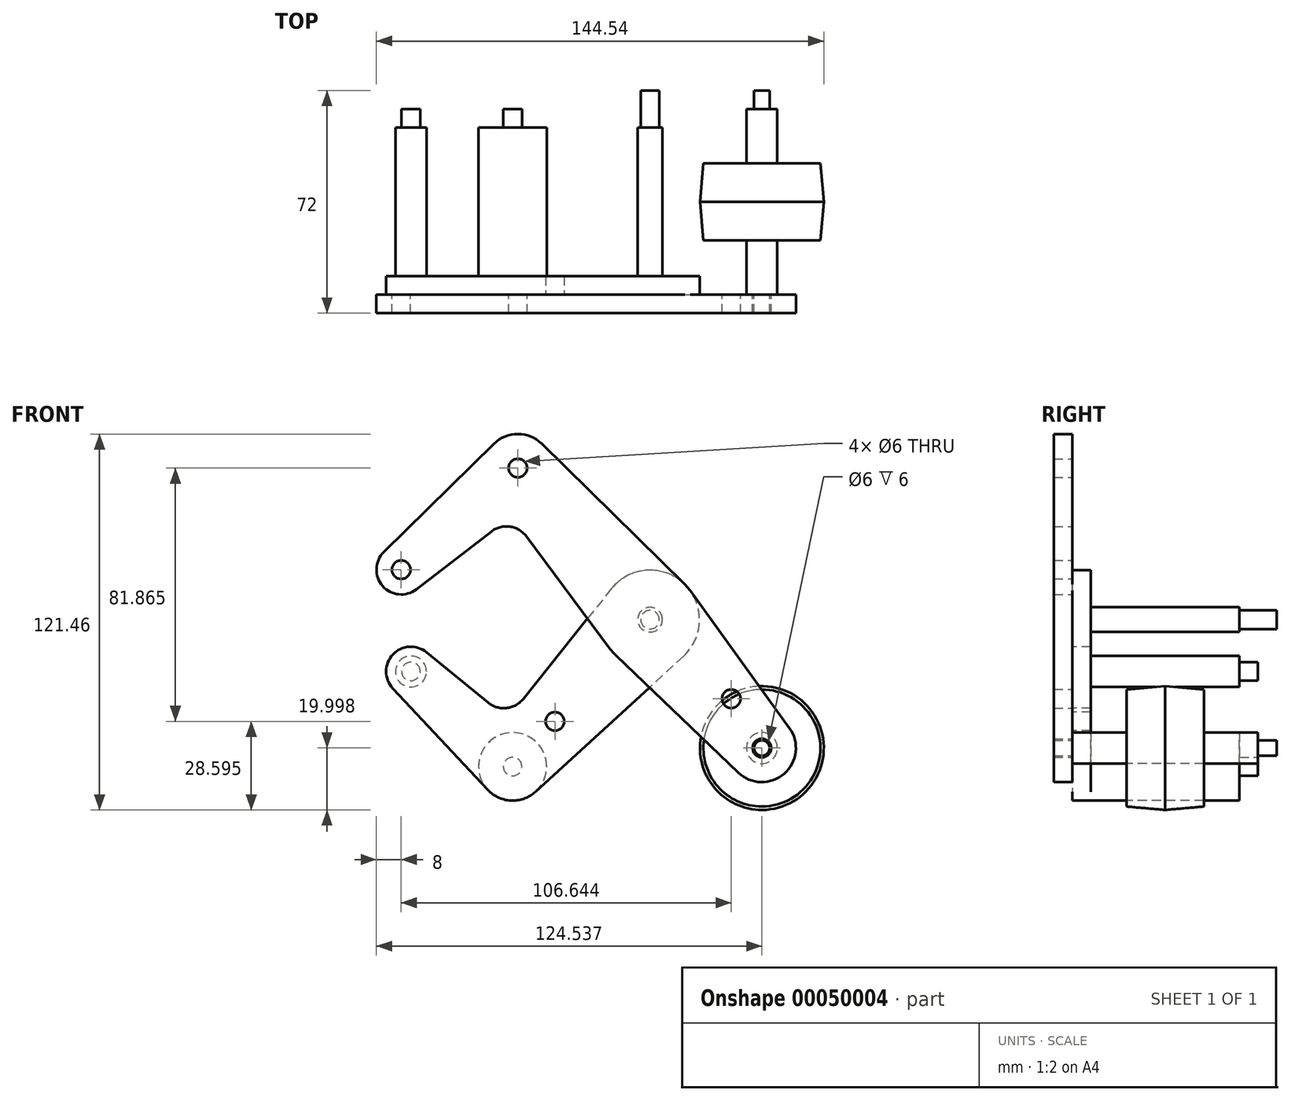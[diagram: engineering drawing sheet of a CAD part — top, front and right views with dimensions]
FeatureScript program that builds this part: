
annotation { "Feature Type Name" : "Feature", "Feature Type Description" : "" }
export const myFeature = defineFeature(function(context is Context, id is Id, definition is map)
    precondition{}
    {
        {
            var Q0;
            Q0=qCreatedBy(makeId("Front.planeOp"),FACE);
            cPlane(context, id + "F0", {"entities" : qUnion([Q0]), "cplaneType" : CPlaneType.OFFSET, "offset" : 30 * mm, "width" : 150 * mm, "height" : 150 * mm});
        }
        {
            var Q0;
            Q0=qCreatedBy(id+"F0.planeOp",FACE);
            var sketch = newSketch(context, id + "F1", { "sketchPlane" : qUnion([Q0])});
            skLineSegment(sketch, "E0", {"start": v(-42.7, 49) * mm, "end": v(36.14, -41.46) * mm, "construction": true});
            skCircle(sketch, "E1", {"center": v(0, 0) * mm, "radius": 3 * mm});
            skCircle(sketch, "E2", {"center": v(36.14, -41.46) * mm, "radius": 3 * mm});
            skCircle(sketch, "E3", {"center": v(-42.7, 49) * mm, "radius": 3 * mm});
            skCircle(sketch, "E4", {"center": v(-80.4, 16.15) * mm, "radius": 3 * mm});
            skLineSegment(sketch, "E5", {"start": v(-42.7, 49) * mm, "end": v(-80.4, 16.15) * mm, "construction": true});
            skCircle(sketch, "E6", {"center": v(36.14, -41.46) * mm, "radius": 11 * mm});
            skCircle(sketch, "E7", {"center": v(-80.4, 16.15) * mm, "radius": 8 * mm});
            skCircle(sketch, "E8", {"center": v(-42.7, 49) * mm, "radius": 11 * mm});
            skLineSegment(sketch, "E9", {"start": v(-86, 21.85) * mm, "end": v(-50.42, 56.84) * mm});
            skLineSegment(sketch, "E10", {"start": v(-75.52, 9.81) * mm, "end": v(-51.3, 28.49) * mm});
            skCircle(sketch, "E11", {"center": v(0, 0) * mm, "radius": 16 * mm});
            skLineSegment(sketch, "E12", {"start": v(-35, 56.84) * mm, "end": v(11.22, 11.4) * mm});
            skLineSegment(sketch, "E13", {"start": v(-40, 26.93) * mm, "end": v(-12.83, -9.55) * mm});
            skLineSegment(sketch, "E14", {"start": v(-11.06, -11.57) * mm, "end": v(28.54, -49.41) * mm});
            skLineSegment(sketch, "E15", {"start": v(12.97, 9.37) * mm, "end": v(45.05, -35.02) * mm});
            skArc(sketch, "E16.filletArc", {"start": v(-40, 26.93) * mm, "mid": v(-45.32, 30.08) * mm, "end": v(-51.3, 28.49) * mm});
            skLineSegment(sketch, "E17", {"start": v(0, 0) * mm, "end": v(-44.4, -47.47) * mm, "construction": true});
            skLineSegment(sketch, "E18", {"start": v(-44.4, -47.47) * mm, "end": v(-77.27, -16.73) * mm, "construction": true});
            skCircle(sketch, "E19", {"center": v(-77.27, -16.73) * mm, "radius": 3 * mm});
            skCircle(sketch, "E20", {"center": v(-44.4, -47.47) * mm, "radius": 3 * mm});
            skCircle(sketch, "E21", {"center": v(-77.27, -16.73) * mm, "radius": 8 * mm});
            skCircle(sketch, "E22", {"center": v(-44.4, -47.47) * mm, "radius": 11 * mm});
            skLineSegment(sketch, "E23", {"start": v(-72.2, -10.54) * mm, "end": v(-52.3, -26.8) * mm});
            skLineSegment(sketch, "E24", {"start": v(-83.1, -22.2) * mm, "end": v(-52.43, -54.99) * mm});
            skLineSegment(sketch, "E25", {"start": v(-12.5, 10) * mm, "end": v(-41, -25.61) * mm});
            skLineSegment(sketch, "E26", {"start": v(10.8, -11.8) * mm, "end": v(-36.97, -55.58) * mm});
            skArc(sketch, "E27.filletArc", {"start": v(-52.3, -26.8) * mm, "mid": v(-46.4, -28.57) * mm, "end": v(-41, -25.61) * mm});
            skCircle(sketch, "E28", {"center": v(-30.74, -32.86) * mm, "radius": 3 * mm});
            skCircle(sketch, "E29", {"center": v(26.24, -25.54) * mm, "radius": 3 * mm});
            skLineSegment(sketch, "E30", {"start": v(26.24, -25.54) * mm, "end": v(23.98, -27.52) * mm, "construction": true});
            skCircle(sketch, "E31", {"center": v(0, 0) * mm, "radius": 4 * mm});
            skCircle(sketch, "E32", {"center": v(-80.4, 16.15) * mm, "radius": 5 * mm});
            skCircle(sketch, "E33", {"center": v(-77.27, -16.73) * mm, "radius": 5 * mm});
            skCircle(sketch, "E34", {"center": v(36.14, -41.46) * mm, "radius": 5 * mm});
            skCircle(sketch, "E35", {"center": v(-44.4, -47.47) * mm, "radius": 5 * mm});
            skSolve(sketch);
        }
        {
            var Q0;
            Q0=makeQuery(id+"F1.imprint","IMPRINT",FACE,{"disambiguationData":[TD([[makeQuery(id+"F1.imprint","IMPRINT",EDGE,{"derivedFrom":sQuery(id+"F1.wireOp",EDGE,"E32")}),-1.0]])]});
            var Q1;
            Q1=makeQuery(id+"F1.imprint","IMPRINT",FACE,{"disambiguationData":[TD([[makeQuery(id+"F1.imprint","IMPRINT",EDGE,{"derivedFrom":sQuery(id+"F1.wireOp",EDGE,"E4")}),-1.0]])]});
            var Q2;
            {var subQ9=sQuery(id+"F1.wireOp",EDGE,"E9");Q2=makeQuery(id+"F1.imprint","IMPRINT",FACE,{"disambiguationData":[TD([[makeQuery(id+"F1.imprint","IMPRINT",EDGE,{"derivedFrom":subQ9}),-1.0]])]});}
            var Q3;
            Q3=makeQuery(id+"F1.imprint","IMPRINT",FACE,{"disambiguationData":[TD([[makeQuery(id+"F1.imprint","IMPRINT",EDGE,{"derivedFrom":sQuery(id+"F1.wireOp",EDGE,"E3")}),-1.0]])]});
            var Q4;
            {var subQ1=sQuery(id+"F1.wireOp",EDGE,"E13");var subQ3=sQuery(id+"F1.wireOp",EDGE,"E11");var subQ5=makeQuery(id+"F1.imprint","INTERSECT",VERTEX,{"derivedFrom":[subQ3,subQ1]});Q4=makeQuery(id+"F1.imprint","IMPRINT",FACE,{"disambiguationData":[TD([[makeQuery(id+"F1.imprint","IMPRINT",EDGE,{"disambiguationData":[TD([[subQ5,1.0]])],"derivedFrom":subQ3}),-1.0]])]});}
            var Q5;
            Q5=makeQuery(id+"F1.imprint","IMPRINT",FACE,{"disambiguationData":[TD([[makeQuery(id+"F1.imprint","IMPRINT",EDGE,{"derivedFrom":sQuery(id+"F1.wireOp",EDGE,"E31")}),-1.0]])]});
            var Q6;
            {var subQ1=sQuery(id+"F1.wireOp",EDGE,"E15");Q6=makeQuery(id+"F1.imprint","IMPRINT",FACE,{"disambiguationData":[TD([[makeQuery(id+"F1.imprint","IMPRINT",EDGE,{"derivedFrom":subQ1}),-1.0]])]});}
            var Q7;
            Q7=makeQuery(id+"F1.imprint","IMPRINT",FACE,{"disambiguationData":[TD([[makeQuery(id+"F1.imprint","IMPRINT",EDGE,{"derivedFrom":sQuery(id+"F1.wireOp",EDGE,"E34")}),-1.0]])]});
            var Q8;
            Q8=makeQuery(id+"F1.imprint","IMPRINT",FACE,{"disambiguationData":[TD([[makeQuery(id+"F1.imprint","IMPRINT",EDGE,{"derivedFrom":sQuery(id+"F1.wireOp",EDGE,"E2")}),-1.0]])]});
            var Q9;
            Q9=makeQuery(id+"F1.imprint","IMPRINT",FACE,{"disambiguationData":[TD([[makeQuery(id+"F1.imprint","IMPRINT",EDGE,{"derivedFrom":sQuery(id+"F1.wireOp",EDGE,"E1")}),-1.0]])]});
            var Q10;
            {var subQ1=sQuery(id+"F1.wireOp",EDGE,"E14");var subQ3=sQuery(id+"F1.wireOp",EDGE,"E11");var subQ5=makeQuery(id+"F1.imprint","INTERSECT",VERTEX,{"derivedFrom":[subQ3,subQ1]});Q10=makeQuery(id+"F1.imprint","IMPRINT",FACE,{"disambiguationData":[TD([[makeQuery(id+"F1.imprint","IMPRINT",EDGE,{"disambiguationData":[TD([[subQ5,-1.0]])],"derivedFrom":subQ3}),-1.0]])]});}
            extrude(context, id + "F2", {"entities" : qUnion([Q0, Q1, Q2, Q3, Q4, Q5, Q6, Q7, Q8, Q9, Q10]), "depth" : 6 * mm});
        }
        {
            var Q0;
            Q0=makeQuery(id+"F1.imprint","IMPRINT",FACE,{"disambiguationData":[TD([[makeQuery(id+"F1.imprint","IMPRINT",EDGE,{"derivedFrom":sQuery(id+"F1.wireOp",EDGE,"E33")}),-1.0]])]});
            var Q1;
            Q1=makeQuery(id+"F1.imprint","IMPRINT",FACE,{"disambiguationData":[TD([[makeQuery(id+"F1.imprint","IMPRINT",EDGE,{"derivedFrom":sQuery(id+"F1.wireOp",EDGE,"E19")}),-1.0]])]});
            var Q2;
            {var subQ2=sQuery(id+"F1.wireOp",EDGE,"E23");Q2=makeQuery(id+"F1.imprint","IMPRINT",FACE,{"disambiguationData":[TD([[makeQuery(id+"F1.imprint","IMPRINT",EDGE,{"derivedFrom":subQ2}),-1.0]])]});}
            var Q3;
            Q3=makeQuery(id+"F1.imprint","IMPRINT",FACE,{"disambiguationData":[TD([[makeQuery(id+"F1.imprint","IMPRINT",EDGE,{"derivedFrom":sQuery(id+"F1.wireOp",EDGE,"E35")}),-1.0]])]});
            var Q4;
            Q4=makeQuery(id+"F1.imprint","IMPRINT",FACE,{"disambiguationData":[TD([[makeQuery(id+"F1.imprint","IMPRINT",EDGE,{"derivedFrom":sQuery(id+"F1.wireOp",EDGE,"E20")}),-1.0]])]});
            var Q5;
            {var subQ1=sQuery(id+"F1.wireOp",EDGE,"E13");var subQ3=sQuery(id+"F1.wireOp",EDGE,"E11");var subQ5=makeQuery(id+"F1.imprint","INTERSECT",VERTEX,{"derivedFrom":[subQ3,subQ1]});Q5=makeQuery(id+"F1.imprint","IMPRINT",FACE,{"disambiguationData":[TD([[makeQuery(id+"F1.imprint","IMPRINT",EDGE,{"disambiguationData":[TD([[subQ5,1.0]])],"derivedFrom":subQ3}),-1.0]])]});}
            var Q6;
            {var subQ1=sQuery(id+"F1.wireOp",EDGE,"E14");var subQ3=sQuery(id+"F1.wireOp",EDGE,"E11");var subQ5=makeQuery(id+"F1.imprint","INTERSECT",VERTEX,{"derivedFrom":[subQ3,subQ1]});Q6=makeQuery(id+"F1.imprint","IMPRINT",FACE,{"disambiguationData":[TD([[makeQuery(id+"F1.imprint","IMPRINT",EDGE,{"disambiguationData":[TD([[subQ5,-1.0]])],"derivedFrom":subQ3}),-1.0]])]});}
            var Q7;
            Q7=makeQuery(id+"F1.imprint","IMPRINT",FACE,{"disambiguationData":[TD([[makeQuery(id+"F1.imprint","IMPRINT",EDGE,{"derivedFrom":sQuery(id+"F1.wireOp",EDGE,"E31")}),-1.0]])]});
            var Q8;
            Q8=makeQuery(id+"F1.imprint","IMPRINT",FACE,{"disambiguationData":[TD([[makeQuery(id+"F1.imprint","IMPRINT",EDGE,{"derivedFrom":sQuery(id+"F1.wireOp",EDGE,"E1")}),-1.0]])]});
            extrude(context, id + "F3", {"entities" : qUnion([Q0, Q1, Q2, Q3, Q4, Q5, Q6, Q7, Q8]), "oppositeDirection" : true, "depth" : 6 * mm});
        }
        {
            var Q0;
            Q0=makeQuery(id+"F1.imprint","IMPRINT",FACE,{"disambiguationData":[TD([[makeQuery(id+"F1.imprint","IMPRINT",EDGE,{"derivedFrom":sQuery(id+"F1.wireOp",EDGE,"E2")}),-1.0]])]});
            var Q1;
            Q1=makeQuery(id+"F1.imprint","IMPRINT",FACE,{"disambiguationData":[TD([[makeQuery(id+"F1.imprint","IMPRINT",EDGE,{"derivedFrom":sQuery(id+"F1.wireOp",EDGE,"E2")}),1.0]])]});
            var Q2;
            Q2=makeQuery(id+"F1.imprint","IMPRINT",FACE,{"disambiguationData":[TD([[makeQuery(id+"F1.imprint","IMPRINT",EDGE,{"derivedFrom":sQuery(id+"F1.wireOp",EDGE,"E1")}),-1.0]])]});
            var Q3;
            Q3=makeQuery(id+"F1.imprint","IMPRINT",FACE,{"disambiguationData":[TD([[makeQuery(id+"F1.imprint","IMPRINT",EDGE,{"derivedFrom":sQuery(id+"F1.wireOp",EDGE,"E1")}),1.0]])]});
            var Q4;
            Q4=qCreatedBy(makeId("Front.planeOp"),FACE);
            var Q5;
            Q5=makeQuery(id+"F2.opExtrude","CAP_FACE",FACE,{"disambiguationData":[OSD([sQuery(id+"F1.wireOp",EDGE,"E1"),sQuery(id+"F1.wireOp",EDGE,"E2"),sQuery(id+"F1.wireOp",EDGE,"E3"),sQuery(id+"F1.wireOp",EDGE,"E4"),sQuery(id+"F1.wireOp",EDGE,"E6"),sQuery(id+"F1.wireOp",EDGE,"E7"),sQuery(id+"F1.wireOp",EDGE,"E8"),sQuery(id+"F1.wireOp",EDGE,"E9"),sQuery(id+"F1.wireOp",EDGE,"E10"),sQuery(id+"F1.wireOp",EDGE,"E11"),sQuery(id+"F1.wireOp",EDGE,"E12"),sQuery(id+"F1.wireOp",EDGE,"E13"),sQuery(id+"F1.wireOp",EDGE,"E14"),sQuery(id+"F1.wireOp",EDGE,"E15"),sQuery(id+"F1.wireOp",EDGE,"E16.filletArc"),sQuery(id+"F1.wireOp",EDGE,"E29")])],"isStart":false});
            extrude(context, id + "F4", {"entities" : qUnion([Q0, Q1, Q2, Q3]), "endBound" : BoundingType.UP_TO_SURFACE, "oppositeDirection" : true, "endBoundEntityFace" : qUnion([Q4]), "depth" : 25 * mm, "hasSecondDirection" : true, "secondDirectionBound" : SecondDirectionBoundingType.UP_TO_SURFACE, "secondDirectionOppositeDirection" : false, "secondDirectionBoundEntityFace" : qUnion([Q5]), "secondDirectionDepth" : 25 * mm});
        }
        {
            var Q0;
            Q0=makeQuery(id+"F1.imprint","IMPRINT",FACE,{"disambiguationData":[TD([[makeQuery(id+"F1.imprint","IMPRINT",EDGE,{"derivedFrom":sQuery(id+"F1.wireOp",EDGE,"E35")}),-1.0]])]});
            var Q1;
            Q1=makeQuery(id+"F1.imprint","IMPRINT",FACE,{"disambiguationData":[TD([[makeQuery(id+"F1.imprint","IMPRINT",EDGE,{"derivedFrom":sQuery(id+"F1.wireOp",EDGE,"E20")}),-1.0]])]});
            var Q2;
            Q2=makeQuery(id+"F1.imprint","IMPRINT",FACE,{"disambiguationData":[TD([[makeQuery(id+"F1.imprint","IMPRINT",EDGE,{"derivedFrom":sQuery(id+"F1.wireOp",EDGE,"E20")}),1.0]])]});
            var Q3;
            Q3=makeQuery(id+"F1.imprint","IMPRINT",FACE,{"disambiguationData":[TD([[makeQuery(id+"F1.imprint","IMPRINT",EDGE,{"derivedFrom":sQuery(id+"F1.wireOp",EDGE,"E19")}),1.0]])]});
            var Q4;
            Q4=makeQuery(id+"F1.imprint","IMPRINT",FACE,{"disambiguationData":[TD([[makeQuery(id+"F1.imprint","IMPRINT",EDGE,{"derivedFrom":sQuery(id+"F1.wireOp",EDGE,"E19")}),-1.0]])]});
            var Q5;
            Q5=qCreatedBy(makeId("Front.planeOp"),FACE);
            extrude(context, id + "F5", {"entities" : qUnion([Q0, Q1, Q2, Q3, Q4]), "endBound" : BoundingType.UP_TO_SURFACE, "oppositeDirection" : true, "endBoundEntityFace" : qUnion([Q5]), "depth" : 25 * mm});
        }
        {
            var Q0;
            Q0=makeQuery(id+"F2.opExtrude","SWEPT_BODY",BODY,{"disambiguationData":[OSD([sQuery(id+"F1.wireOp",EDGE,"E1"),sQuery(id+"F1.wireOp",EDGE,"E2"),sQuery(id+"F1.wireOp",EDGE,"E3"),sQuery(id+"F1.wireOp",EDGE,"E4"),sQuery(id+"F1.wireOp",EDGE,"E6"),sQuery(id+"F1.wireOp",EDGE,"E7"),sQuery(id+"F1.wireOp",EDGE,"E8"),sQuery(id+"F1.wireOp",EDGE,"E9"),sQuery(id+"F1.wireOp",EDGE,"E10"),sQuery(id+"F1.wireOp",EDGE,"E11"),sQuery(id+"F1.wireOp",EDGE,"E12"),sQuery(id+"F1.wireOp",EDGE,"E13"),sQuery(id+"F1.wireOp",EDGE,"E14"),sQuery(id+"F1.wireOp",EDGE,"E15"),sQuery(id+"F1.wireOp",EDGE,"E16.filletArc"),sQuery(id+"F1.wireOp",EDGE,"E29")])]});
            var Q1;
            Q1=makeQuery(id+"F3.opExtrude","SWEPT_BODY",BODY,{"disambiguationData":[OSD([sQuery(id+"F1.wireOp",EDGE,"E1"),sQuery(id+"F1.wireOp",EDGE,"E11"),sQuery(id+"F1.wireOp",EDGE,"E19"),sQuery(id+"F1.wireOp",EDGE,"E20"),sQuery(id+"F1.wireOp",EDGE,"E21"),sQuery(id+"F1.wireOp",EDGE,"E22"),sQuery(id+"F1.wireOp",EDGE,"E23"),sQuery(id+"F1.wireOp",EDGE,"E24"),sQuery(id+"F1.wireOp",EDGE,"E25"),sQuery(id+"F1.wireOp",EDGE,"E26"),sQuery(id+"F1.wireOp",EDGE,"E27.filletArc"),sQuery(id+"F1.wireOp",EDGE,"E28")])]});
            var Q2;
            Q2=makeQuery(id+"F5.opExtrude","SWEPT_BODY",BODY,{"disambiguationData":[OSD([sQuery(id+"F1.wireOp",EDGE,"E33")])]});
            var Q3;
            Q3=makeQuery(id+"F5.opExtrude","SWEPT_BODY",BODY,{"disambiguationData":[OSD([sQuery(id+"F1.wireOp",EDGE,"E22")])]});
            var Q4;
            Q4=makeQuery(id+"F4.opExtrude","SWEPT_BODY",BODY,{"disambiguationData":[OSD([sQuery(id+"F1.wireOp",EDGE,"E31")])]});
            var Q5;
            Q5=makeQuery(id+"F4.opExtrude","SWEPT_BODY",BODY,{"disambiguationData":[OSD([sQuery(id+"F1.wireOp",EDGE,"E34")])]});
            var Q6;
            Q6=makeQuery(id+"F2.opExtrude","SWEPT_FACE",FACE,{"disambiguationData":[OSD([sQuery(id+"F1.wireOp",EDGE,"E2")])]});
            booleanBodies(context, id + "F6", {"operationType" : BooleanOperationType.SUBTRACTION, "tools" : qUnion([Q0, Q1]), "targets" : qUnion([Q2, Q3, Q4, Q5]), "offset" : true, "entitiesToOffset" : qUnion([Q6]), "offsetDistance" : 0.5 * mm, "keepTools" : true});
        }
        {
            var Q0;
            Q0=makeQuery(id+"F5.opExtrude","SWEPT_BODY",BODY,{"disambiguationData":[OSD([sQuery(id+"F1.wireOp",EDGE,"E33")])]});
            var Q1;
            Q1=makeQuery(id+"F4.opExtrude","SWEPT_BODY",BODY,{"disambiguationData":[OSD([sQuery(id+"F1.wireOp",EDGE,"E31")])]});
            var Q2;
            Q2=makeQuery(id+"F5.opExtrude","SWEPT_BODY",BODY,{"disambiguationData":[OSD([sQuery(id+"F1.wireOp",EDGE,"E22")])]});
            var Q3;
            Q3=makeQuery(id+"F4.opExtrude","SWEPT_BODY",BODY,{"disambiguationData":[OSD([sQuery(id+"F1.wireOp",EDGE,"E34")])]});
            var Q4;
            Q4=qCreatedBy(makeId("Front.planeOp"),FACE);
            mirror(context, id + "F7", {"operationType" : NewBodyOperationType.ADD, "entities" : qUnion([Q0, Q1, Q2, Q3]), "mirrorPlane" : qUnion([Q4])});
        }
        {
            var Q0;
            Q0=qCreatedBy(makeId("Front.planeOp"),FACE);
            var sketch = newSketch(context, id + "F8", { "sketchPlane" : qUnion([Q0])});
            skCircle(sketch, "E36", {"center": v(36.14, -41.46) * mm, "radius": 20 * mm});
            skSolve(sketch);
        }
        {
            var Q0;
            Q0=qSketchRegion(id+"F8",true);
            extrude(context, id + "F9", {"entities" : qUnion([Q0]), "endBound" : BoundingType.SYMMETRIC, "depth" : 25 * mm, "hasDraft" : true, "draftAngle" : 5 * degree, "draftPullDirection" : true});
        }
    });
